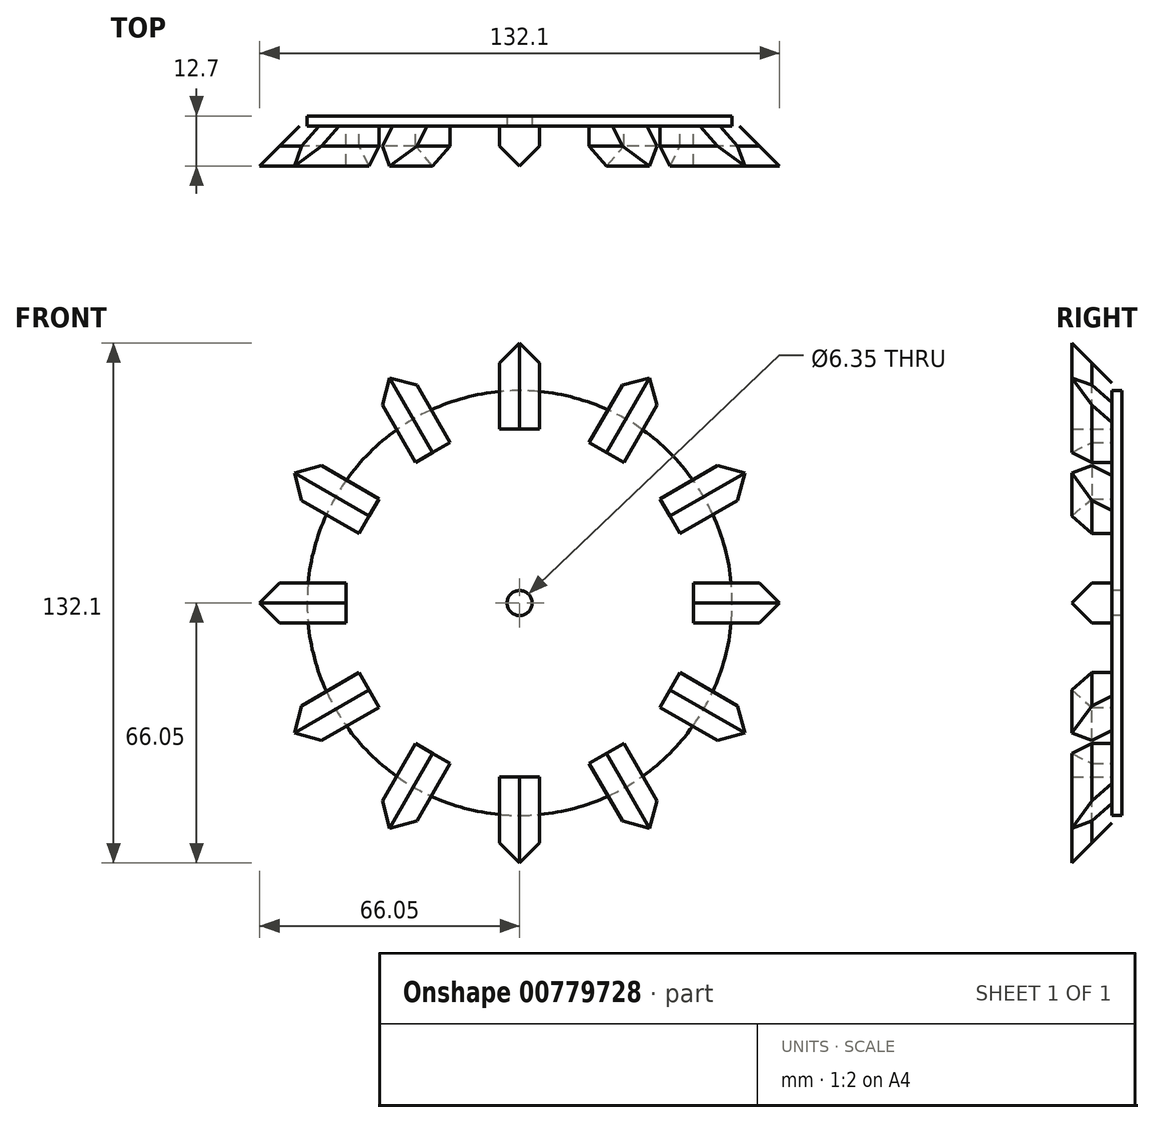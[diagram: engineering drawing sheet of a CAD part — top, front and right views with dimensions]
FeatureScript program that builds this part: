
annotation { "Feature Type Name" : "Feature", "Feature Type Description" : "" }
export const myFeature = defineFeature(function(context is Context, id is Id, definition is map)
    precondition{}
    {
        {
            var Q0;
            Q0=qCreatedBy(makeId("Front.planeOp"),FACE);
            var sketch = newSketch(context, id + "F0", { "sketchPlane" : qUnion([Q0])});
            skCircle(sketch, "E0", {"center": v(0, 0) * mm, "radius": 53.97 * mm});
            skSolve(sketch);
        }
        {
            var Q0;
            Q0=makeQuery(id+"F0.imprint","IMPRINT",FACE,{"disambiguationData":[TD([[makeQuery(id+"F0.imprint","IMPRINT",EDGE,{"derivedFrom":sQuery(id+"F0.wireOp",EDGE,"E0")}),1.0]])]});
            var sketch = newSketch(context, id + "F1", { "sketchPlane" : qUnion([Q0])});
            skLineSegment(sketch, "E1.bottom", {"start": v(-5.08, 66.05) * mm, "end": v(5.08, 66.05) * mm});
            skLineSegment(sketch, "E1.top", {"start": v(-5.08, 44.15) * mm, "end": v(5.08, 44.15) * mm});
            skLineSegment(sketch, "E1.left", {"start": v(-5.08, 66.05) * mm, "end": v(-5.08, 44.15) * mm});
            skLineSegment(sketch, "E1.right", {"start": v(5.08, 66.05) * mm, "end": v(5.08, 44.15) * mm});
            skSolve(sketch);
        }
        {
            var Q0;
            Q0 = qSketchRegion(id + "F1", true);
            extrude(context, id + "F2", {"entities" : qUnion([Q0]), "depth" : 10.16 * mm, "offsetDistance" : 25.4 * mm});
        }
        {
            var Q0;
            Q0=makeQuery(id+"F2.opExtrude","CAP_EDGE",EDGE,{"disambiguationData":[OSD([sQuery(id+"F1.wireOp",EDGE,"E1.left")])],"isStart":false});
            var Q1;
            Q1=makeQuery(id+"F2.opExtrude","CAP_EDGE",EDGE,{"disambiguationData":[OSD([sQuery(id+"F1.wireOp",EDGE,"E1.right")])],"isStart":false});
            chamfer(context, id + "F3", {"entities" : qUnion([Q0, Q1]), "width" : 5.08 * mm, "tangentPropagation" : true});
        }
        {
            var Q0;
            Q0=makeQuery(id+"F2.opExtrude","CAP_EDGE",EDGE,{"disambiguationData":[OSD([sQuery(id+"F1.wireOp",EDGE,"E1.bottom")])],"isStart":true});
            chamfer(context, id + "F4", {"entities" : qUnion([Q0]), "width" : 10.16 * mm, "tangentPropagation" : true});
        }
        {
            var Q0;
            Q0=makeQuery(id+"F2.opExtrude","SWEPT_BODY",BODY,{"disambiguationData":[OSD([sQuery(id+"F1.wireOp",EDGE,"E1.bottom"),sQuery(id+"F1.wireOp",EDGE,"E1.top"),sQuery(id+"F1.wireOp",EDGE,"E1.left"),sQuery(id+"F1.wireOp",EDGE,"E1.right")])]});
            var Q1;
            Q1=sQuery(id+"F0.wireOp",EDGE,"E0");
            circularPattern(context, id + "F5", {"entities" : qUnion([Q0]), "axis" : qUnion([Q1]), "angle" : 360 * degree, "instanceCount" : 12, "equalSpace" : true});
        }
        {
            var Q0;
            Q0 = qSketchRegion(id + "F0", true);
            extrude(context, id + "F6", {"entities" : qUnion([Q0]), "oppositeDirection" : true, "depth" : 2.54 * mm, "offsetDistance" : 25.4 * mm});
        }
        {
            var Q0;
            Q0=makeQuery(id+"F6.opExtrude","CAP_FACE",FACE,{"disambiguationData":[OSD([sQuery(id+"F0.wireOp",EDGE,"E0")])],"isStart":true});
            var sketch = newSketch(context, id + "F7", { "sketchPlane" : qUnion([Q0])});
            skCircle(sketch, "E2", {"center": v(0, 0) * mm, "radius": 3.18 * mm});
            skSolve(sketch);
        }
        {
            var Q0;
            Q0 = qSketchRegion(id + "F7", true);
            extrude(context, id + "F8", {"entities" : qUnion([Q0]), "operationType" : NewBodyOperationType.REMOVE, "oppositeDirection" : true, "depth" : 25.4 * mm, "offsetDistance" : 25.4 * mm});
        }
    });
